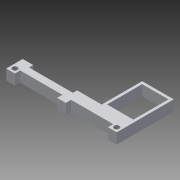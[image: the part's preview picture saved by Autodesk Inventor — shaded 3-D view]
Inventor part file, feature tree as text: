
AUTODESK INVENTOR PART (.ipt)
format: ipt  version: 2013 (Build 170138000, 138)  size: 101,888 bytes
history: native  units: mm
features: extrude x1, sketch x1
ambient origin geometry x8: Origin, YZ Plane, XZ Plane, XY Plane, X Axis, Y Axis, Z Axis, Center Point
bodies: Solid1 (feature_tree)
feature tree (2):
  extrude  "Extrusion1"  [1 undecoded]
  sketch  "Sketch1"  dims[d0=6.0mm d1=0.0mm]
note: 1 required parameter value undecoded (feature->parameter linkage not recoverable at this tier; creation-order binding heuristic only, values carry confidence <= 0.55)
